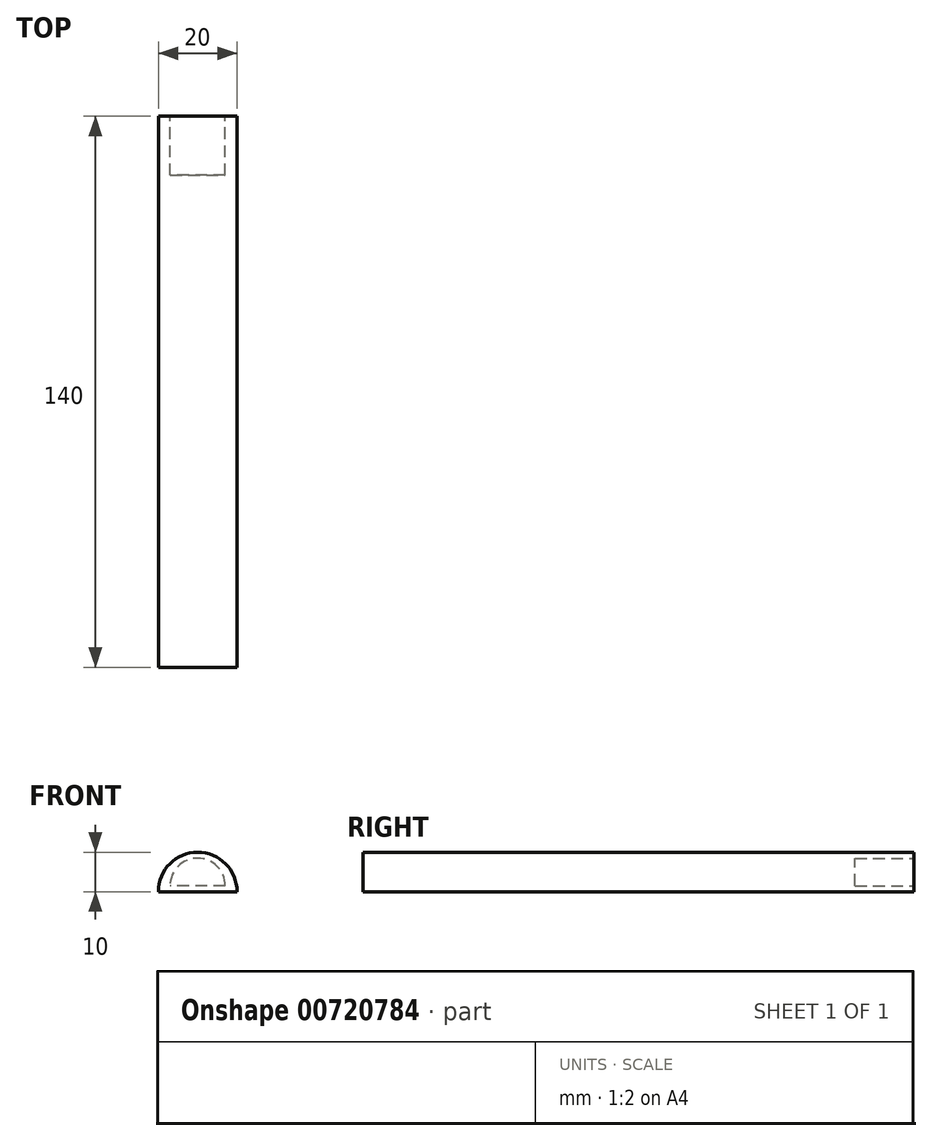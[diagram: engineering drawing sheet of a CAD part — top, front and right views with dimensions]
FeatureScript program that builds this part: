
annotation { "Feature Type Name" : "Feature", "Feature Type Description" : "" }
export const myFeature = defineFeature(function(context is Context, id is Id, definition is map)
    precondition{}
    {
        {
            var Q0;
            Q0=qCreatedBy(makeId("Front.planeOp"),FACE);
            var sketch = newSketch(context, id + "F0", { "sketchPlane" : qUnion([Q0])});
            skLineSegment(sketch, "E0", {"start": v(0, 0) * mm, "end": v(10, 0) * mm});
            skLineSegment(sketch, "E1", {"start": v(0, 5) * mm, "end": v(0, 0) * mm});
            skLineSegment(sketch, "E2", {"start": v(10, 0) * mm, "end": v(10, 5) * mm});
            skLineSegment(sketch, "E3", {"start": v(10, 5) * mm, "end": v(0, 5) * mm});
            skArc(sketch, "E4", {"start": v(10, 0) * mm, "mid": v(5, 5) * mm, "end": v(0, 0) * mm});
            skLineSegment(sketch, "E5", {"start": v(0, 0) * mm, "end": v(-5, 0) * mm});
            skArc(sketch, "E6", {"start": v(-5, 0) * mm, "mid": v(5, 10) * mm, "end": v(15, 0) * mm});
            skLineSegment(sketch, "E7", {"start": v(10, 0) * mm, "end": v(15, 0) * mm});
            skSolve(sketch);
        }
        {
            var Q0;
            {var subQ1=sQuery(id+"F0.wireOp",EDGE,"E1");Q0=makeQuery(id+"F0.imprint","IMPRINT",FACE,{"disambiguationData":[TD([[makeQuery(id+"F0.imprint","IMPRINT",EDGE,{"derivedFrom":subQ1}),-1.0]])]});}
            var Q1;
            {var subQ0=sQuery(id+"F0.wireOp",EDGE,"E0");Q1=makeQuery(id+"F0.imprint","IMPRINT",FACE,{"disambiguationData":[TD([[makeQuery(id+"F0.imprint","IMPRINT",EDGE,{"derivedFrom":subQ0}),1.0]])]});}
            var Q2;
            {var subQ0=sQuery(id+"F0.wireOp",EDGE,"E1");Q2=makeQuery(id+"F0.imprint","IMPRINT",FACE,{"disambiguationData":[TD([[makeQuery(id+"F0.imprint","IMPRINT",EDGE,{"derivedFrom":subQ0}),1.0]])]});}
            var Q3;
            {var subQ0=sQuery(id+"F0.wireOp",EDGE,"E2");Q3=makeQuery(id+"F0.imprint","IMPRINT",FACE,{"disambiguationData":[TD([[makeQuery(id+"F0.imprint","IMPRINT",EDGE,{"derivedFrom":subQ0}),1.0]])]});}
            extrude(context, id + "F1", {"entities" : qUnion([Q0, Q1, Q2, Q3]), "depth" : 15 * mm, "offsetDistance" : 25 * mm});
        }
        {
            var Q0;
            {var subQ1=sQuery(id+"F0.wireOp",EDGE,"E1");Q0=makeQuery(id+"F0.imprint","IMPRINT",FACE,{"disambiguationData":[TD([[makeQuery(id+"F0.imprint","IMPRINT",EDGE,{"derivedFrom":subQ1}),-1.0]])]});}
            var Q1;
            {var subQ0=sQuery(id+"F0.wireOp",EDGE,"E2");Q1=makeQuery(id+"F0.imprint","IMPRINT",FACE,{"disambiguationData":[TD([[makeQuery(id+"F0.imprint","IMPRINT",EDGE,{"derivedFrom":subQ0}),1.0]])]});}
            var Q2;
            {var subQ0=sQuery(id+"F0.wireOp",EDGE,"E1");Q2=makeQuery(id+"F0.imprint","IMPRINT",FACE,{"disambiguationData":[TD([[makeQuery(id+"F0.imprint","IMPRINT",EDGE,{"derivedFrom":subQ0}),1.0]])]});}
            var Q3;
            Q3=makeQuery(id+"F1.opExtrude","CAP_FACE",FACE,{"disambiguationData":[OSD([sQuery(id+"F0.wireOp",EDGE,"E0"),sQuery(id+"F0.wireOp",EDGE,"E4")])],"isStart":true});
            extrude(context, id + "F2", {"entities" : qUnion([Q0, Q1, Q2, Q3]), "operationType" : NewBodyOperationType.ADD, "oppositeDirection" : true, "depth" : 125 * mm, "offsetDistance" : 25 * mm});
        }
        {
            var Q0;
            {var subQ0=sQuery(id+"F0.wireOp",EDGE,"E4");Q0=makeQuery(id+"F2.boolean.opBoolean","MERGE",FACE,{"derivedFrom":[makeQuery(id+"F2.opExtrude","CAP_FACE",FACE,{"disambiguationData":[OSD([subQ0,sQuery(id+"F0.wireOp",EDGE,"E5"),sQuery(id+"F0.wireOp",EDGE,"E6"),sQuery(id+"F0.wireOp",EDGE,"E7")])],"isStart":false}),makeQuery(id+"F2.opExtrude","CAP_FACE",FACE,{"disambiguationData":[OSD([sQuery(id+"F0.wireOp",EDGE,"E0"),subQ0])],"isStart":false})]});}
            var sketch = newSketch(context, id + "F3", { "sketchPlane" : qUnion([Q0])});
            skLineSegment(sketch, "E8", {"start": v(-5, 0) * mm, "end": v(-5, 1.5) * mm, "construction": true});
            skLineSegment(sketch, "E9", {"start": v(-5, 1.5) * mm, "end": v(7.35, 1.5) * mm, "construction": true});
            skArc(sketch, "E10", {"start": v(2, 1.5) * mm, "mid": v(-5, 8.5) * mm, "end": v(-12, 1.5) * mm});
            skLineSegment(sketch, "E11", {"start": v(-12, 1.5) * mm, "end": v(2, 1.5) * mm});
            skSolve(sketch);
        }
        {
            var Q0;
            Q0=makeQuery(id+"F3.imprint","IMPRINT",FACE,{"disambiguationData":[TD([[makeQuery(id+"F3.imprint","IMPRINT",EDGE,{"derivedFrom":sQuery(id+"F3.wireOp",EDGE,"E10")}),1.0]])]});
            extrude(context, id + "F4", {"entities" : qUnion([Q0]), "operationType" : NewBodyOperationType.REMOVE, "oppositeDirection" : true, "depth" : 15 * mm, "offsetDistance" : 25 * mm});
        }
    });
